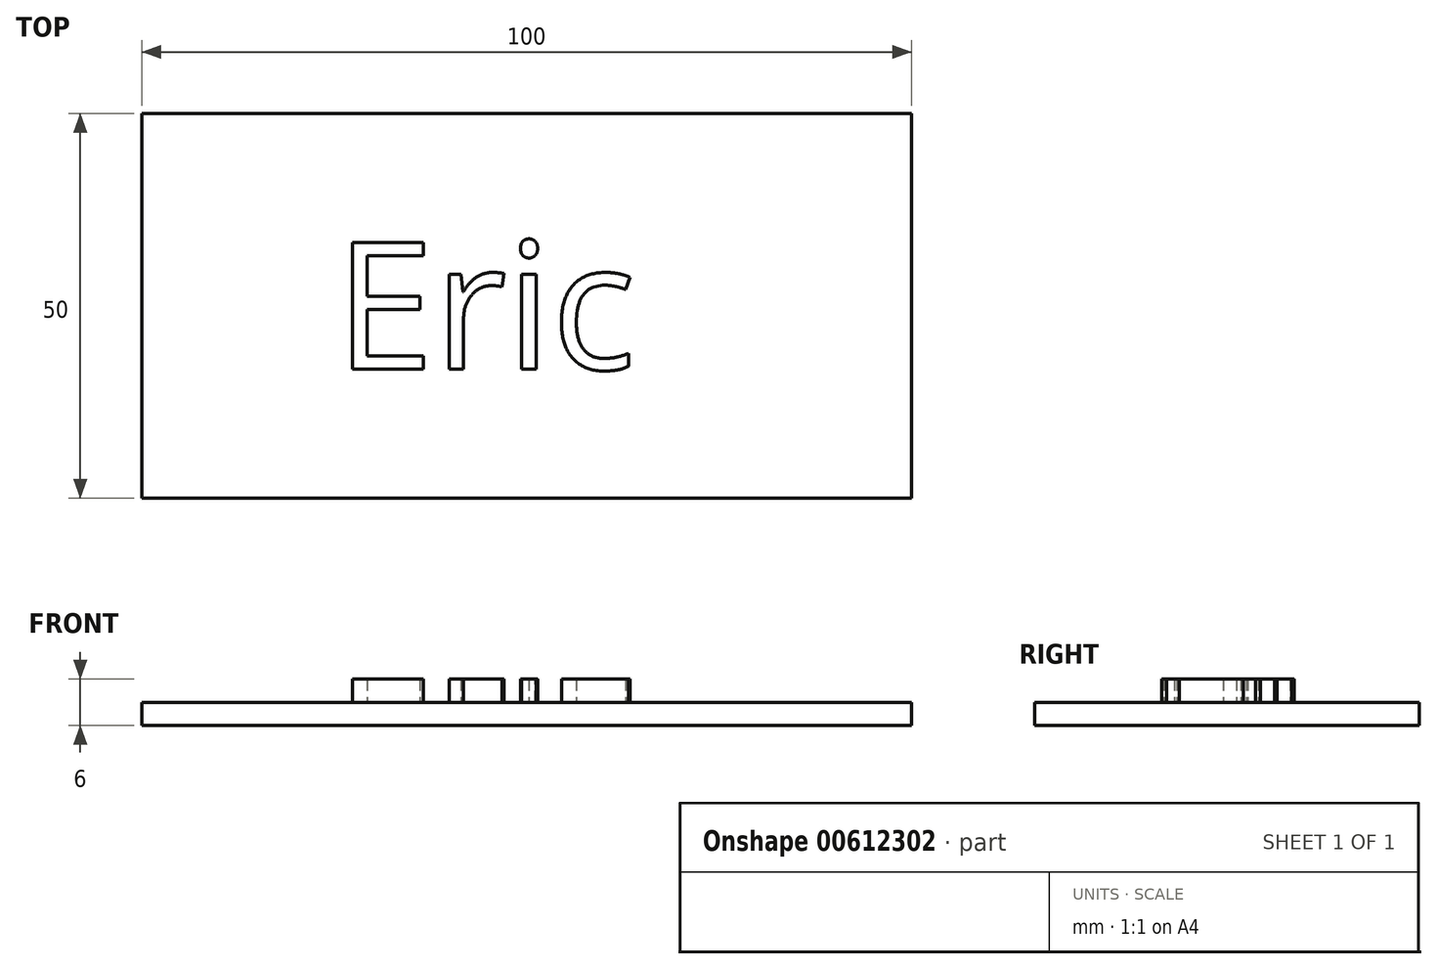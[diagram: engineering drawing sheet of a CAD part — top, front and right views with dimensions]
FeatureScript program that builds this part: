
annotation { "Feature Type Name" : "Feature", "Feature Type Description" : "" }
export const myFeature = defineFeature(function(context is Context, id is Id, definition is map)
    precondition{}
    {
        {
            var Q0;
            Q0=qCreatedBy(makeId("Top.planeOp"),FACE);
            var sketch = newSketch(context, id + "F0", { "sketchPlane" : qUnion([Q0])});
            skLineSegment(sketch, "E0.bottom", {"start": v(0, 0) * mm, "end": v(100, 0) * mm});
            skLineSegment(sketch, "E0.top", {"start": v(0, 50) * mm, "end": v(100, 50) * mm});
            skLineSegment(sketch, "E0.left", {"start": v(0, 0) * mm, "end": v(0, 50) * mm});
            skLineSegment(sketch, "E0.right", {"start": v(100, 0) * mm, "end": v(100, 50) * mm});
            skSolve(sketch);
        }
        {
            var Q0;
            Q0 = qSketchRegion(id + "F0", true);
            extrude(context, id + "F1", {"entities" : qUnion([Q0]), "depth" : 3 * mm, "offsetDistance" : 25 * mm});
        }
        {
            var Q0;
            Q0=makeQuery(id+"F1.opExtrude","CAP_FACE",FACE,{"disambiguationData":[OSD([sQuery(id+"F0.wireOp",EDGE,"E0.bottom"),sQuery(id+"F0.wireOp",EDGE,"E0.top"),sQuery(id+"F0.wireOp",EDGE,"E0.left"),sQuery(id+"F0.wireOp",EDGE,"E0.right")])],"isStart":false});
            var sketch = newSketch(context, id + "F2", { "sketchPlane" : qUnion([Q0])});
            skText(sketch, "E1", { "text": "Eric", "fontName": "OpenSans-Regular.ttf"});
            const initialGuessF2  = {"E1": [0.0251, 0.01676, 1, 0, 0.01663]};
            skSetInitialGuess(sketch, initialGuessF2);
            skSolve(sketch);
        }
        {
            var Q0;
            Q0 = qSketchRegion(id + "F2", true);
            extrude(context, id + "F3", {"entities" : qUnion([Q0]), "operationType" : NewBodyOperationType.ADD, "depth" : 3 * mm, "offsetDistance" : 25 * mm});
        }
    });
